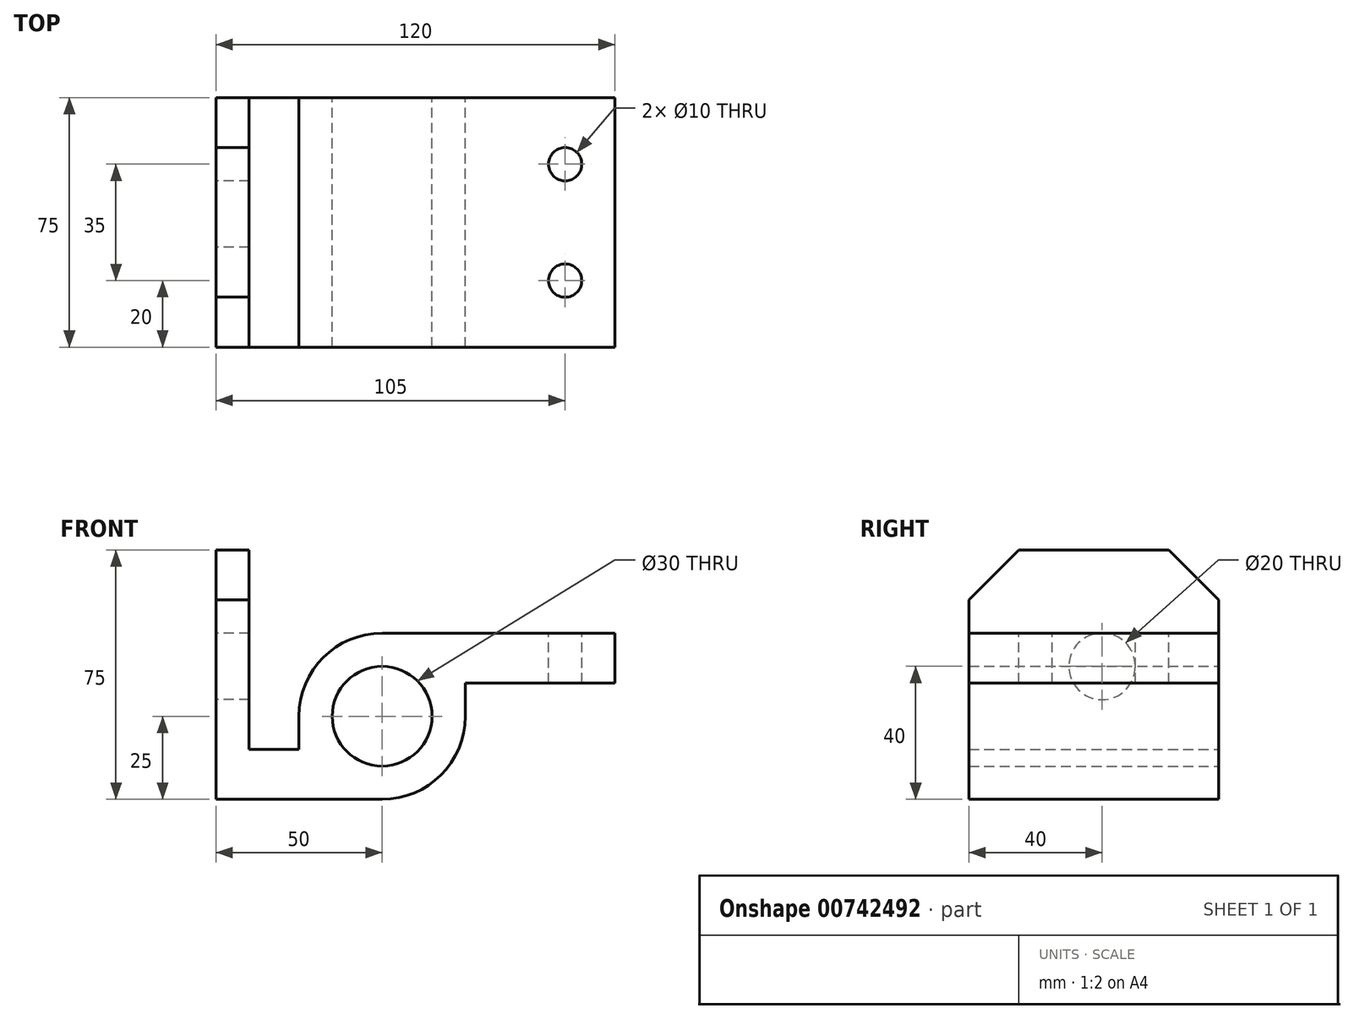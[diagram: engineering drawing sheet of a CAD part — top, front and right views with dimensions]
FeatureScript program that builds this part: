
annotation { "Feature Type Name" : "Feature", "Feature Type Description" : "" }
export const myFeature = defineFeature(function(context is Context, id is Id, definition is map)
    precondition{}
    {
        {
            var Q0;
            Q0=qCreatedBy(makeId("Front.planeOp"),FACE);
            var sketch = newSketch(context, id + "F0", { "sketchPlane" : qUnion([Q0])});
            skArc(sketch, "E0", {"start": v(0, 25) * mm, "mid": v(-17.68, 17.68) * mm, "end": v(-25, 0) * mm});
            skCircle(sketch, "E1", {"center": v(0, 0) * mm, "radius": 15 * mm});
            skLineSegment(sketch, "E2", {"start": v(0, -25) * mm, "end": v(-50, -25) * mm});
            skLineSegment(sketch, "E3", {"start": v(-50, -25) * mm, "end": v(-50, 50) * mm});
            skLineSegment(sketch, "E4", {"start": v(0, 25) * mm, "end": v(70, 25) * mm});
            skLineSegment(sketch, "E5", {"start": v(70, 25) * mm, "end": v(70, 10) * mm});
            skLineSegment(sketch, "E6", {"start": v(70, 10) * mm, "end": v(25, 10) * mm});
            skLineSegment(sketch, "E7", {"start": v(25, 10) * mm, "end": v(25, 0) * mm});
            skLineSegment(sketch, "E8", {"start": v(-50, 50) * mm, "end": v(-40, 50) * mm});
            skLineSegment(sketch, "E9", {"start": v(-40, 50) * mm, "end": v(-40, -10) * mm});
            skLineSegment(sketch, "E10", {"start": v(-40, -10) * mm, "end": v(-25, -10) * mm});
            skLineSegment(sketch, "E11", {"start": v(-25, -10) * mm, "end": v(-25, 0) * mm});
            skArc(sketch, "E12.trimOffspring", {"start": v(0, -25) * mm, "mid": v(17.68, -17.68) * mm, "end": v(25, 0) * mm});
            skSolve(sketch);
        }
        {
            var Q0;
            Q0=makeQuery(id+"F0.imprint","IMPRINT",FACE,{"disambiguationData":[TD([[makeQuery(id+"F0.imprint","IMPRINT",EDGE,{"derivedFrom":sQuery(id+"F0.wireOp",EDGE,"E0")}),1.0]])]});
            extrude(context, id + "F1", {"entities" : qUnion([Q0]), "depth" : 75 * mm, "offsetDistance" : 25 * mm});
        }
        {
            var Q0;
            Q0=makeQuery(id+"F1.opExtrude","SWEPT_FACE",FACE,{"disambiguationData":[OSD([sQuery(id+"F0.wireOp",EDGE,"E3")])]});
            var sketch = newSketch(context, id + "F2", { "sketchPlane" : qUnion([Q0])});
            skLineSegment(sketch, "E13", {"start": v(15, 50) * mm, "end": v(0, 35) * mm});
            skLineSegment(sketch, "E14", {"start": v(60, 50) * mm, "end": v(75, 35) * mm});
            skCircle(sketch, "E15", {"center": v(35, 15) * mm, "radius": 10 * mm});
            skSolve(sketch);
        }
        {
            var Q0;
            {var subQ0=sQuery(id+"F2.wireOp",EDGE,"E13");Q0=makeQuery(id+"F2.imprint","IMPRINT",FACE,{"disambiguationData":[TD([[makeQuery(id+"F2.imprint","IMPRINT",EDGE,{"derivedFrom":subQ0}),-1.0]])]});}
            var Q1;
            {var subQ0=sQuery(id+"F2.wireOp",EDGE,"E14");Q1=makeQuery(id+"F2.imprint","IMPRINT",FACE,{"disambiguationData":[TD([[makeQuery(id+"F2.imprint","IMPRINT",EDGE,{"derivedFrom":subQ0}),1.0]])]});}
            var Q2;
            Q2=makeQuery(id+"F2.imprint","IMPRINT",FACE,{"disambiguationData":[TD([[makeQuery(id+"F2.imprint","IMPRINT",EDGE,{"derivedFrom":sQuery(id+"F2.wireOp",EDGE,"E15")}),1.0]])]});
            extrude(context, id + "F3", {"entities" : qUnion([Q0, Q1, Q2]), "operationType" : NewBodyOperationType.REMOVE, "oppositeDirection" : true, "depth" : 10 * mm, "offsetDistance" : 25 * mm});
        }
        {
            var Q0;
            Q0=makeQuery(id+"F1.opExtrude","SWEPT_FACE",FACE,{"disambiguationData":[OSD([sQuery(id+"F0.wireOp",EDGE,"E4")])]});
            var sketch = newSketch(context, id + "F4", { "sketchPlane" : qUnion([Q0])});
            skCircle(sketch, "E16", {"center": v(55, -20) * mm, "radius": 5 * mm});
            skCircle(sketch, "E17", {"center": v(55, -55) * mm, "radius": 5 * mm});
            skSolve(sketch);
        }
        {
            var Q0;
            Q0=makeQuery(id+"F4.imprint","IMPRINT",FACE,{"disambiguationData":[TD([[makeQuery(id+"F4.imprint","IMPRINT",EDGE,{"derivedFrom":sQuery(id+"F4.wireOp",EDGE,"E16")}),1.0]])]});
            var Q1;
            Q1=makeQuery(id+"F4.imprint","IMPRINT",FACE,{"disambiguationData":[TD([[makeQuery(id+"F4.imprint","IMPRINT",EDGE,{"derivedFrom":sQuery(id+"F4.wireOp",EDGE,"E17")}),1.0]])]});
            extrude(context, id + "F5", {"entities" : qUnion([Q0, Q1]), "operationType" : NewBodyOperationType.REMOVE, "oppositeDirection" : true, "depth" : 15 * mm, "offsetDistance" : 25 * mm});
        }
    });
